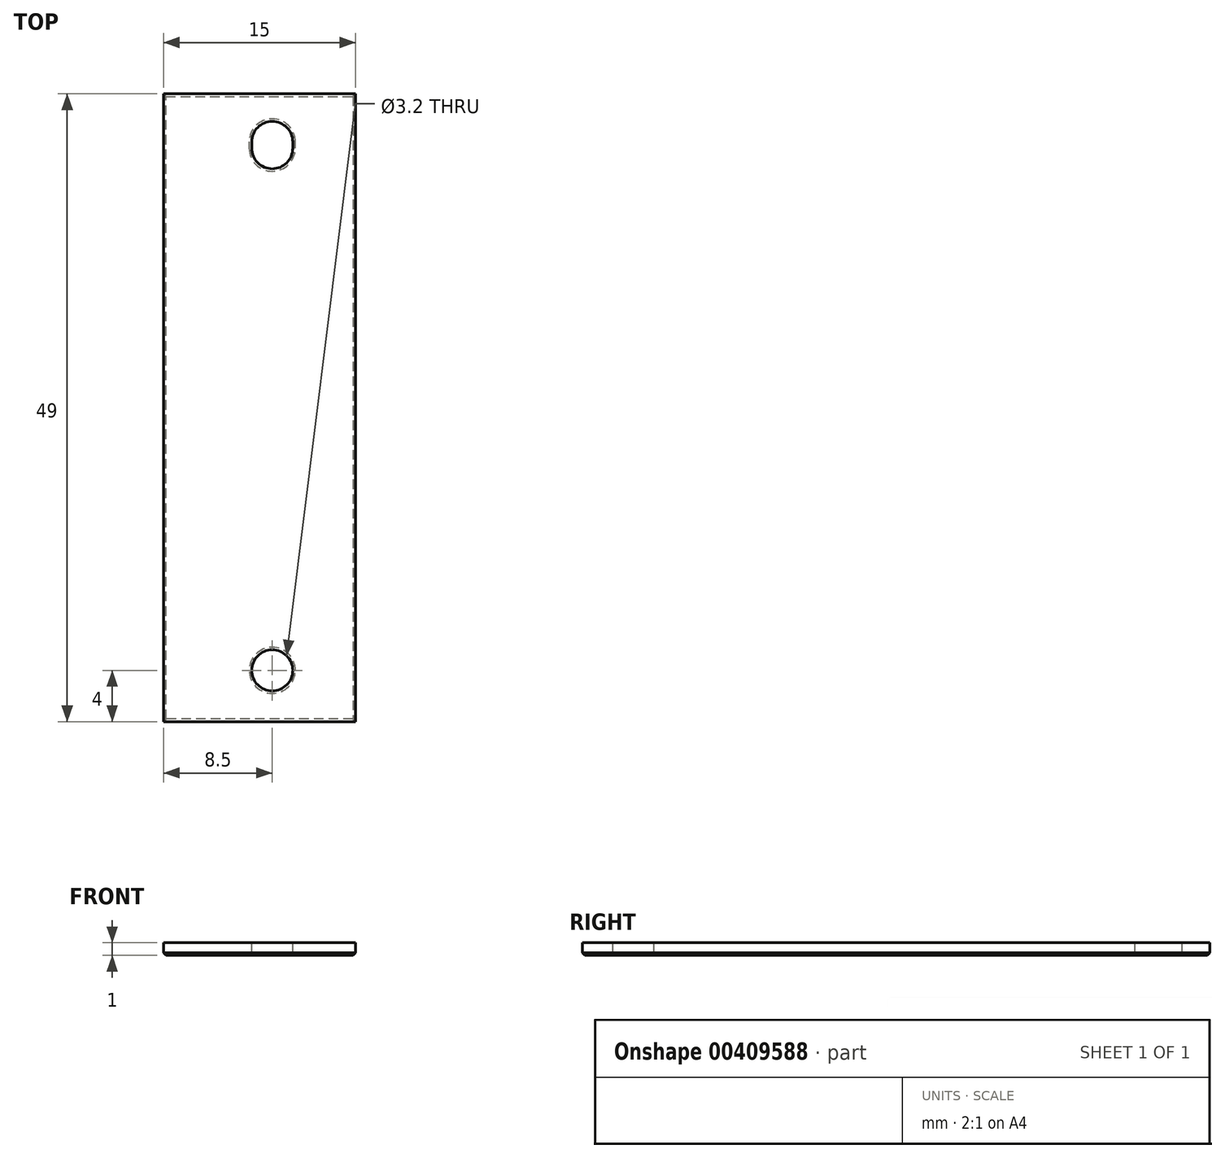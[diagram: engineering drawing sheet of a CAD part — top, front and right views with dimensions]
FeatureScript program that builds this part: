
annotation { "Feature Type Name" : "Feature", "Feature Type Description" : "" }
export const myFeature = defineFeature(function(context is Context, id is Id, definition is map)
    precondition{}
    {
        {
            var Q0;
            Q0=qCreatedBy(makeId("Top.planeOp"),FACE);
            var sketch = newSketch(context, id + "F0", { "sketchPlane" : qUnion([Q0])});
            skLineSegment(sketch, "E0.bottom", {"start": v(6.5, 24.5) * mm, "end": v(-8.5, 24.5) * mm});
            skLineSegment(sketch, "E0.top", {"start": v(6.5, -24.5) * mm, "end": v(-8.5, -24.5) * mm});
            skLineSegment(sketch, "E0.left", {"start": v(6.5, 24.5) * mm, "end": v(6.5, -24.5) * mm});
            skLineSegment(sketch, "E0.right", {"start": v(-8.5, 24.5) * mm, "end": v(-8.5, -24.5) * mm});
            skPoint(sketch, "E0.middle", {"position": v(0, 0) * mm});
            skLineSegment(sketch, "E1", {"start": v(0, 20.5) * mm, "end": v(0, -20.5) * mm, "construction": true});
            skCircle(sketch, "E2", {"center": v(0, -20.5) * mm, "radius": 1.6 * mm});
            skLineSegment(sketch, "E3", {"start": v(0, 20.75) * mm, "end": v(0, 20.25) * mm, "construction": true});
            skArc(sketch, "E4.0.startCap", {"start": v(-1.6, 20.75) * mm, "mid": v(0, 22.35) * mm, "end": v(1.6, 20.75) * mm});
            skArc(sketch, "E4.0.endCap", {"start": v(1.6, 20.25) * mm, "mid": v(0, 18.65) * mm, "end": v(-1.6, 20.25) * mm});
            skLineSegment(sketch, "E4.0.left", {"start": v(1.6, 20.75) * mm, "end": v(1.6, 20.25) * mm});
            skLineSegment(sketch, "E4.0.right", {"start": v(-1.6, 20.75) * mm, "end": v(-1.6, 20.25) * mm});
            skSolve(sketch);
        }
        {
            var Q0;
            Q0=qCreatedBy(makeId("Front.planeOp"),FACE);
            var sketch = newSketch(context, id + "F1", { "sketchPlane" : qUnion([Q0])});
            skLineSegment(sketch, "E5", {"start": v(0, 0) * mm, "end": v(0, 1) * mm});
            skSolve(sketch);
        }
        {
            var Q0;
            Q0 = qSketchRegion(id + "F0", true);
            var Q1;
            Q1=sQuery(id+"F1.wireOp",EDGE,"E5");
            sweep(context, id + "F2", {"profiles" : qUnion([Q0]), "path" : qUnion([Q1])});
        }
        {
            var Q0;
            Q0=makeQuery(id+"F2.opSweep","CAP_FACE",FACE,{"disambiguationData":[OSD([sQuery(id+"F0.wireOp",EDGE,"E0.bottom"),sQuery(id+"F0.wireOp",EDGE,"E0.top"),sQuery(id+"F0.wireOp",EDGE,"E0.left"),sQuery(id+"F0.wireOp",EDGE,"E0.right"),sQuery(id+"F0.wireOp",EDGE,"E2"),sQuery(id+"F0.wireOp",EDGE,"E4.0.startCap"),sQuery(id+"F0.wireOp",EDGE,"E4.0.endCap"),sQuery(id+"F0.wireOp",EDGE,"E4.0.left"),sQuery(id+"F0.wireOp",EDGE,"E4.0.right"),sQuery(id+"F1.wireOp",VERTEX,"E5.start")])],"isStart":true});
            chamfer(context, id + "F3", {"entities" : qUnion([Q0]), "width" : 0.2 * mm});
        }
    });
